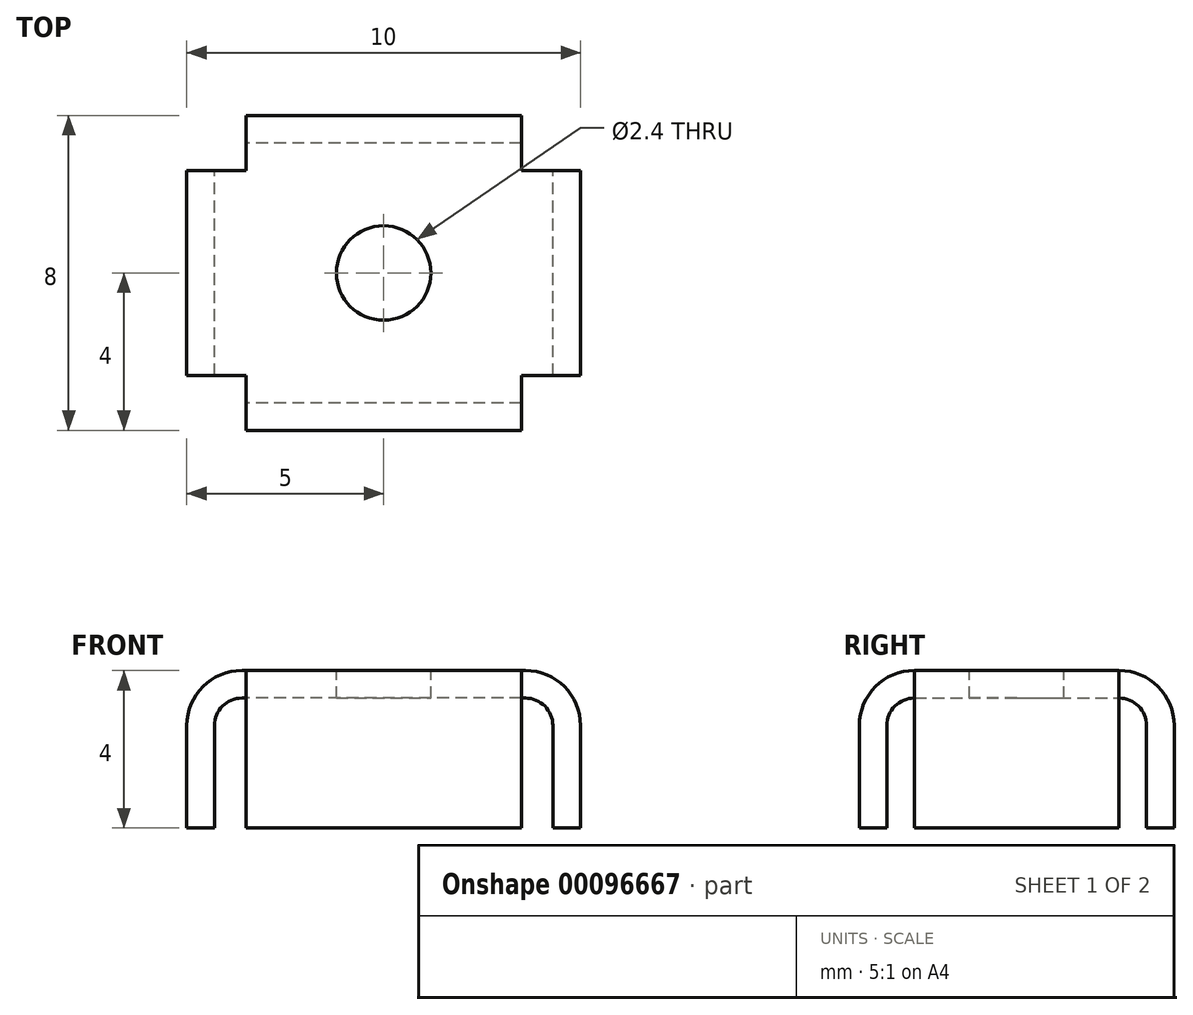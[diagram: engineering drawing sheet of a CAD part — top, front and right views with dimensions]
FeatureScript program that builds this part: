
annotation { "Feature Type Name" : "Feature", "Feature Type Description" : "" }
export const myFeature = defineFeature(function(context is Context, id is Id, definition is map)
    precondition{}
    {
        {
            var Q0;
            Q0=qCreatedBy(makeId("Front.planeOp"),FACE);
            var sketch = newSketch(context, id + "F0", { "sketchPlane" : qUnion([Q0])});
            skLineSegment(sketch, "E0.bottom", {"start": v(3.6, -0.35) * mm, "end": v(-3.6, -0.35) * mm});
            skLineSegment(sketch, "E0.top", {"start": v(3.6, 0.35) * mm, "end": v(-3.6, 0.35) * mm});
            skPoint(sketch, "E0.middle", {"position": v(0, 0) * mm});
            skLineSegment(sketch, "E1.top", {"start": v(4.3, -3.65) * mm, "end": v(5, -3.65) * mm});
            skLineSegment(sketch, "E1.left", {"start": v(4.3, -1.05) * mm, "end": v(4.3, -3.65) * mm});
            skLineSegment(sketch, "E1.right", {"start": v(5, -1.05) * mm, "end": v(5, -3.65) * mm});
            skArc(sketch, "E2", {"start": v(3.6, -0.35) * mm, "mid": v(4.1, -0.56) * mm, "end": v(4.3, -1.05) * mm});
            skArc(sketch, "E3", {"start": v(5, -1.05) * mm, "mid": v(4.59, -0.06) * mm, "end": v(3.6, 0.35) * mm});
            skLineSegment(sketch, "E4", {"start": v(0, 0) * mm, "end": v(0, -4.6) * mm, "construction": true});
            skLineSegment(sketch, "E5.MirrorCS", {"start": v(-4.3, -3.65) * mm, "end": v(-5, -3.65) * mm});
            skLineSegment(sketch, "E6.MirrorCS", {"start": v(-4.3, -1.05) * mm, "end": v(-4.3, -3.65) * mm});
            skArc(sketch, "E7.MirrorCS", {"start": v(-3.6, -0.35) * mm, "mid": v(-4.1, -0.56) * mm, "end": v(-4.3, -1.05) * mm});
            skArc(sketch, "E8.MirrorCS", {"start": v(-5, -1.05) * mm, "mid": v(-4.59, -0.06) * mm, "end": v(-3.6, 0.35) * mm});
            skLineSegment(sketch, "E9.MirrorCS", {"start": v(-5, -1.05) * mm, "end": v(-5, -3.65) * mm});
            skSolve(sketch);
        }
        {
            var Q0;
            Q0=qSketchRegion(id+"F0",true);
            extrude(context, id + "F1", {"entities" : qUnion([Q0]), "endBound" : BoundingType.SYMMETRIC, "depth" : 5.2 * mm});
        }
        {
            var Q0;
            Q0=qCreatedBy(makeId("Right.planeOp"),FACE);
            var sketch = newSketch(context, id + "F2", { "sketchPlane" : qUnion([Q0])});
            skLineSegment(sketch, "E10.bottom", {"start": v(-3.3, -3.65) * mm, "end": v(-4, -3.65) * mm});
            skLineSegment(sketch, "E10.left", {"start": v(-3.3, -3.65) * mm, "end": v(-3.3, -1.05) * mm});
            skLineSegment(sketch, "E10.right", {"start": v(-4, -3.65) * mm, "end": v(-4, -1.05) * mm});
            skArc(sketch, "E11", {"start": v(-2.6, -0.35) * mm, "mid": v(-3.1, -0.56) * mm, "end": v(-3.3, -1.05) * mm});
            skArc(sketch, "E12", {"start": v(-2.6, 0.35) * mm, "mid": v(-3.59, -0.06) * mm, "end": v(-4, -1.05) * mm});
            skLineSegment(sketch, "E13", {"start": v(-2.6, -0.35) * mm, "end": v(2.6, -0.35) * mm, "construction": true});
            skLineSegment(sketch, "E14", {"start": v(-2.6, 0.35) * mm, "end": v(2.6, 0.35) * mm, "construction": true});
            skLineSegment(sketch, "E15", {"start": v(-2.6, 0.35) * mm, "end": v(-2.6, -0.35) * mm});
            skLineSegment(sketch, "E16", {"start": v(0, 0) * mm, "end": v(0, -3.07) * mm, "construction": true});
            skLineSegment(sketch, "E17.MirrorCS", {"start": v(2.6, 0.35) * mm, "end": v(2.6, -0.35) * mm});
            skArc(sketch, "E18.MirrorCS", {"start": v(2.6, 0.35) * mm, "mid": v(3.59, -0.06) * mm, "end": v(4, -1.05) * mm});
            skArc(sketch, "E19.MirrorCS", {"start": v(2.6, -0.35) * mm, "mid": v(3.1, -0.56) * mm, "end": v(3.3, -1.05) * mm});
            skLineSegment(sketch, "E20.MirrorCS", {"start": v(3.3, -3.65) * mm, "end": v(3.3, -1.05) * mm});
            skLineSegment(sketch, "E21.MirrorCS", {"start": v(4, -3.65) * mm, "end": v(4, -1.05) * mm});
            skLineSegment(sketch, "E22.MirrorCS", {"start": v(3.3, -3.65) * mm, "end": v(4, -3.65) * mm});
            skSolve(sketch);
        }
        {
            var Q0;
            Q0=makeQuery(id+"F2.imprint","IMPRINT",FACE,{"disambiguationData":[TD([[makeQuery(id+"F2.imprint","IMPRINT",EDGE,{"derivedFrom":sQuery(id+"F2.wireOp",EDGE,"E10.bottom")}),-1.0]])]});
            var Q1;
            Q1=makeQuery(id+"F2.imprint","IMPRINT",FACE,{"disambiguationData":[TD([[makeQuery(id+"F2.imprint","IMPRINT",EDGE,{"derivedFrom":sQuery(id+"F2.wireOp",EDGE,"E17.MirrorCS")}),1.0]])]});
            extrude(context, id + "F3", {"entities" : qUnion([Q0, Q1]), "operationType" : NewBodyOperationType.ADD, "endBound" : BoundingType.SYMMETRIC, "depth" : 7 * mm});
        }
        {
            var Q0;
            Q0=makeQuery(id+"F1.opExtrude","SWEPT_FACE",FACE,{"disambiguationData":[OSD([sQuery(id+"F0.wireOp",EDGE,"E0.top")])]});
            var sketch = newSketch(context, id + "F4", { "sketchPlane" : qUnion([Q0])});
            skPoint(sketch, "E23", {"position": v(0, 0) * mm});
            skSolve(sketch);
        }
        {
            var Q0;
            Q0=sQuery(id+"F4.wireOp",VERTEX,"E23");
            var Q1;
            Q1=makeQuery(id+"F1.opExtrude","SWEPT_BODY",BODY,{"disambiguationData":[OSD([sQuery(id+"F0.wireOp",EDGE,"E0.bottom"),sQuery(id+"F0.wireOp",EDGE,"E0.top"),sQuery(id+"F0.wireOp",EDGE,"E1.top"),sQuery(id+"F0.wireOp",EDGE,"E1.left"),sQuery(id+"F0.wireOp",EDGE,"E1.right"),sQuery(id+"F0.wireOp",EDGE,"E2"),sQuery(id+"F0.wireOp",EDGE,"E3"),sQuery(id+"F0.wireOp",EDGE,"E5.MirrorCS"),sQuery(id+"F0.wireOp",EDGE,"E6.MirrorCS"),sQuery(id+"F0.wireOp",EDGE,"E7.MirrorCS"),sQuery(id+"F0.wireOp",EDGE,"E8.MirrorCS"),sQuery(id+"F0.wireOp",EDGE,"E9.MirrorCS")])]});
            hole(context, id + "F5", {"style" : HoleStyle.SIMPLE, "endStyle" : HoleEndStyle.THROUGH, "standardTappedOrClearance" : lookupTablePath({ "standard" : "ISO", "engagement" : "75%", "pitch" : "0.6 mm", "size" : "M3", "type" : "Tapped" }), "standardBlindInLast" : lookupTablePath({ "standard" : "ISO", "engagement" : "75%", "pitch" : "0.6 mm", "size" : "M3", "type" : "Tapped" }), "holeDiameter" : 2.4 * mm, "locations" : qUnion([Q0]), "scope" : qUnion([Q1]), "isTappedThrough" : true, "showTappedDepth" : true});
        }
    });
